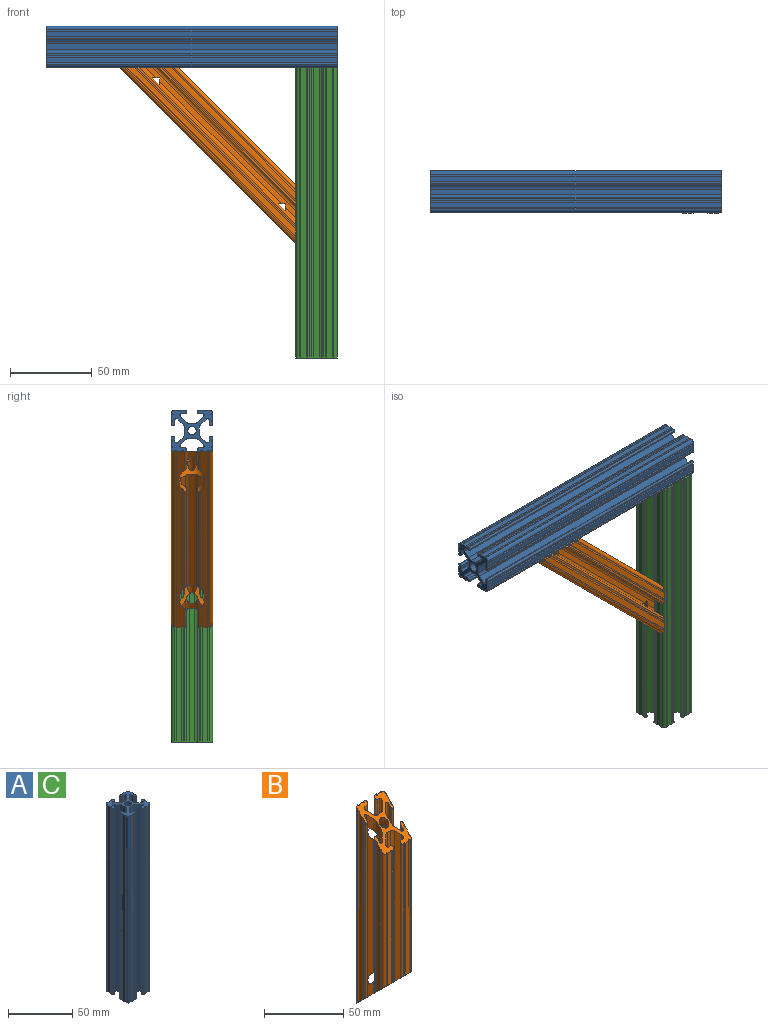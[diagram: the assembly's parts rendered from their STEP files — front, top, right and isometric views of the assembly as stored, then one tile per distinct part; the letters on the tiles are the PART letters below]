
ASSEMBLY  parts=3 mates=6
PART A: 99 faces, bbox 25.4x25.4x177.8 mm
  f0: cylinder r=2.6mm len=177.8mm, axis (0,0,-1), area 2908.5mm2, adj f97,f98
  f1: cylinder r=2.11mm len=177.8mm, axis (0,0,-1), area 597.8mm2, adj f88,f89,f97,f98
  f2: cylinder r=2.11mm len=177.8mm, axis (0,0,-1), area 597.8mm2, adj f65,f66,f97,f98
  f3: cylinder r=1.03mm len=177.8mm, axis (0,0,-1), area 433.3mm2, adj f57,f58,f97,f98
  f4: cylinder r=0.51mm len=177.8mm, axis (0,0,-1), area 283.7mm2, adj f42,f43,f97,f98
  f5: cylinder r=0.51mm len=177.8mm, axis (0,0,-1), area 283.8mm2, adj f41,f42,f97,f98
  f6: cylinder r=0.51mm len=177.8mm, axis (0,0,-1), area 283.8mm2, adj f24,f25,f97,f98
  f7: cylinder r=0.51mm len=177.8mm, axis (0,0,-1), area 283.7mm2, adj f23,f24,f97,f98
  f8: cylinder r=1.08mm len=177.8mm, axis (0,0,-1), area 452.8mm2, adj f9,f96,f97,f98
  f9: plane 177.8x3.23mm, normal (0.71,-0.71,0), area 810.8mm2, adj f8,f10,f97,f98
  f10: cylinder r=3.17mm len=177.8mm, axis (0,0,-1), area 442.9mm2, adj f9,f11,f97,f98
  f11: plane 177.8x3.42mm, normal (0,-1,0), area 607.8mm2, adj f10,f12,f97,f98
  f12: cylinder r=3.17mm len=177.8mm, axis (0,0,-1), area 442.9mm2, adj f11,f13,f97,f98
  f13: plane 177.8x3.23mm, normal (-0.71,-0.71,0), area 810.8mm2, adj f12,f14,f97,f98
  f14: cylinder r=1.08mm len=177.8mm, axis (0,0,-1), area 452.8mm2, adj f13,f15,f97,f98
  f15: plane 177.8x2.13mm, normal (0,1,0), area 378.5mm2, adj f14,f16,f97,f98
  f16: cylinder r=1.05mm len=177.8mm, axis (0,0,-1), area 293mm2, adj f15,f17,f97,f98
  f17: plane 177.8x0.11mm, normal (-1,0,0), area 19.9mm2, adj f16,f18,f97,f98
  f18: cylinder r=1.05mm len=177.8mm, axis (0,0,-1), area 293mm2, adj f17,f19,f97,f98
  f19: plane 177.8x1.03mm, normal (0,-1,0), area 183.1mm2, adj f18,f20,f97,f98
  f20: cylinder r=0.51mm len=177.8mm, axis (0,0,-1), area 283.8mm2, adj f19,f21,f97,f98
  f21: plane 177.8x3.22mm, normal (0,-1,0), area 572mm2, adj f20,f22,f97,f98
  f22: cylinder r=0.51mm len=177.8mm, axis (0,0,-1), area 283.7mm2, adj f21,f23,f97,f98
  f23: cylinder r=2.11mm len=177.8mm, axis (0,0,-1), area 597.8mm2, adj f7,f22,f97,f98
  f24: plane 177.8x3.22mm, normal (1,0,0), area 572mm2, adj f6,f7,f97,f98
  f25: plane 177.8x1.03mm, normal (1,0,0), area 183.1mm2, adj f6,f26,f97,f98
  f26: cylinder r=1.05mm len=177.8mm, axis (0,0,-1), area 293mm2, adj f25,f27,f97,f98
  f27: plane 177.8x0.11mm, normal (0,1,0), area 19.9mm2, adj f26,f28,f97,f98
  f28: cylinder r=1.05mm len=177.8mm, axis (0,0,-1), area 293mm2, adj f27,f29,f97,f98
  f29: plane 177.8x2.11mm, normal (-1,0,0), area 376mm2, adj f28,f30,f97,f98
  f30: cylinder r=1.03mm len=177.8mm, axis (0,0,-1), area 430.2mm2, adj f29,f31,f97,f98
  f31: plane 177.8x3.3mm, normal (0.71,0.71,0), area 827.9mm2, adj f30,f32,f97,f98
  f32: cylinder r=3.17mm len=177.8mm, axis (0,0,-1), area 444mm2, adj f31,f33,f97,f98
  f33: plane 177.8x3.19mm, normal (1,0,0), area 566.5mm2, adj f32,f34,f97,f98
  f34: cylinder r=3.17mm len=177.8mm, axis (0,0,-1), area 444mm2, adj f33,f35,f97,f98
  f35: plane 177.8x3.3mm, normal (0.71,-0.71,0), area 827.9mm2, adj f34,f36,f97,f98
  f36: cylinder r=1.03mm len=177.8mm, axis (0,0,-1), area 430.2mm2, adj f35,f37,f97,f98
  f37: plane 177.8x2.11mm, normal (-1,0,0), area 376mm2, adj f36,f38,f97,f98
  f38: cylinder r=1.05mm len=177.8mm, axis (0,0,-1), area 293mm2, adj f37,f39,f97,f98
  f39: plane 177.8x0.11mm, normal (0,-1,0), area 19.9mm2, adj f38,f40,f97,f98
  f40: cylinder r=1.05mm len=177.8mm, axis (0,0,-1), area 293mm2, adj f39,f41,f97,f98
  f41: plane 177.8x1.03mm, normal (1,0,0), area 183.1mm2, adj f5,f40,f97,f98
  f42: plane 177.8x3.22mm, normal (1,0,0), area 572mm2, adj f4,f5,f97,f98
  f43: cylinder r=2.11mm len=177.8mm, axis (0,0,-1), area 597.8mm2, adj f4,f44,f97,f98
  f44: cylinder r=0.51mm len=177.8mm, axis (0,0,-1), area 283.7mm2, adj f43,f45,f97,f98
  f45: plane 177.8x3.22mm, normal (0,1,0), area 572mm2, adj f44,f46,f97,f98
  f46: cylinder r=0.51mm len=177.8mm, axis (0,0,-1), area 283.8mm2, adj f45,f47,f97,f98
  f47: plane 177.8x1.03mm, normal (0,1,0), area 183.1mm2, adj f46,f48,f97,f98
  f48: cylinder r=1.05mm len=177.8mm, axis (0,0,-1), area 293mm2, adj f47,f49,f97,f98
  f49: plane 177.8x0.11mm, normal (-1,0,0), area 19.9mm2, adj f48,f50,f97,f98
  f50: cylinder r=1.05mm len=177.8mm, axis (0,0,-1), area 293mm2, adj f49,f51,f97,f98
  f51: plane 177.8x2.19mm, normal (0,-1,0), area 389.3mm2, adj f50,f52,f97,f98
  f52: cylinder r=1.03mm len=177.8mm, axis (0,0,-1), area 433.3mm2, adj f51,f53,f97,f98
  f53: plane 177.8x3.31mm, normal (-0.71,0.71,0), area 831mm2, adj f52,f54,f97,f98
  f54: cylinder r=3.17mm len=177.8mm, axis (0,0,-1), area 442.7mm2, adj f53,f55,f97,f98
  f55: plane 177.8x3.31mm, normal (0,1,0), area 588.8mm2, adj f54,f56,f97,f98
  f56: cylinder r=3.17mm len=177.8mm, axis (0,0,-1), area 442.7mm2, adj f55,f57,f97,f98
  f57: plane 177.8x3.31mm, normal (0.71,0.71,0), area 831mm2, adj f3,f56,f97,f98
  f58: plane 177.8x2.19mm, normal (0,-1,0), area 389.3mm2, adj f3,f59,f97,f98
  f59: cylinder r=1.05mm len=177.8mm, axis (0,0,-1), area 293mm2, adj f58,f60,f97,f98
  f60: plane 177.8x0.11mm, normal (1,0,0), area 19.9mm2, adj f59,f61,f97,f98
  f61: cylinder r=1.05mm len=177.8mm, axis (0,0,-1), area 293mm2, adj f60,f62,f97,f98
  f62: plane 177.8x1.03mm, normal (0,1,0), area 183.1mm2, adj f61,f63,f97,f98
  f63: cylinder r=0.51mm len=177.8mm, axis (0,0,-1), area 283.8mm2, adj f62,f64,f97,f98
  f64: plane 177.8x3.22mm, normal (0,1,0), area 572mm2, adj f63,f65,f97,f98
  f65: cylinder r=0.51mm len=177.8mm, axis (0,0,-1), area 283.7mm2, adj f2,f64,f97,f98
  f66: cylinder r=0.51mm len=177.8mm, axis (0,0,-1), area 283.7mm2, adj f2,f67,f97,f98
  f67: plane 177.8x3.22mm, normal (-1,0,0), area 572mm2, adj f66,f68,f97,f98
  f68: cylinder r=0.51mm len=177.8mm, axis (0,0,-1), area 283.8mm2, adj f67,f69,f97,f98
  f69: plane 177.8x1.03mm, normal (-1,0,0), area 183.1mm2, adj f68,f70,f97,f98
  f70: cylinder r=1.05mm len=177.8mm, axis (0,0,-1), area 293mm2, adj f69,f71,f97,f98
  f71: plane 177.8x0.11mm, normal (0,-1,0), area 19.9mm2, adj f70,f72,f97,f98
  f72: cylinder r=1.05mm len=177.8mm, axis (0,0,-1), area 293mm2, adj f71,f73,f97,f98
  f73: plane 177.8x2.11mm, normal (1,0,0), area 376mm2, adj f72,f74,f97,f98
  f74: cylinder r=1.03mm len=177.8mm, axis (0,0,-1), area 430.2mm2, adj f73,f75,f97,f98
  f75: plane 177.8x3.3mm, normal (-0.71,-0.71,0), area 827.9mm2, adj f74,f76,f97,f98
  f76: cylinder r=3.17mm len=177.8mm, axis (0,0,-1), area 444mm2, adj f75,f77,f97,f98
  f77: plane 177.8x3.19mm, normal (-1,0,0), area 566.5mm2, adj f76,f78,f97,f98
  f78: cylinder r=3.17mm len=177.8mm, axis (0,0,-1), area 444mm2, adj f77,f79,f97,f98
  f79: plane 177.8x3.3mm, normal (-0.71,0.71,0), area 827.9mm2, adj f78,f80,f97,f98
  f80: cylinder r=1.03mm len=177.8mm, axis (0,0,-1), area 430.2mm2, adj f79,f81,f97,f98
  f81: plane 177.8x2.11mm, normal (1,0,0), area 376mm2, adj f80,f82,f97,f98
  f82: cylinder r=1.05mm len=177.8mm, axis (0,0,-1), area 293mm2, adj f81,f83,f97,f98
  f83: plane 177.8x0.11mm, normal (0,1,0), area 19.9mm2, adj f82,f84,f97,f98
  f84: cylinder r=1.05mm len=177.8mm, axis (0,0,-1), area 293mm2, adj f83,f85,f97,f98
  f85: plane 177.8x1.03mm, normal (-1,0,0), area 183.1mm2, adj f84,f86,f97,f98
  f86: cylinder r=0.51mm len=177.8mm, axis (0,0,-1), area 283.8mm2, adj f85,f87,f97,f98
  f87: plane 177.8x3.22mm, normal (-1,0,0), area 572mm2, adj f86,f88,f97,f98
  f88: cylinder r=0.51mm len=177.8mm, axis (0,0,-1), area 283.7mm2, adj f1,f87,f97,f98
  f89: cylinder r=0.51mm len=177.8mm, axis (0,0,-1), area 283.7mm2, adj f1,f90,f97,f98
  f90: plane 177.8x3.22mm, normal (0,-1,0), area 572mm2, adj f89,f91,f97,f98
  f91: cylinder r=0.51mm len=177.8mm, axis (0,0,-1), area 283.8mm2, adj f90,f92,f97,f98
  f92: plane 177.8x1.03mm, normal (0,-1,0), area 183.1mm2, adj f91,f93,f97,f98
  f93: cylinder r=1.05mm len=177.8mm, axis (0,0,-1), area 293mm2, adj f92,f94,f97,f98
  f94: plane 177.8x0.11mm, normal (1,0,0), area 19.9mm2, adj f93,f95,f97,f98
  f95: cylinder r=1.05mm len=177.8mm, axis (0,0,-1), area 293mm2, adj f94,f96,f97,f98
  f96: plane 177.8x2.13mm, normal (0,1,0), area 378.5mm2, adj f8,f95,f97,f98
  f97: plane 25.4x25.4mm, normal (0,0,-1), area 280.1mm2, adj f0,f1,f2,f3,f4,f5,f6,f7
  f98: plane 25.4x25.4mm, normal (0,0,1), area 280.1mm2, adj f0,f1,f2,f3,f4,f5,f6,f7
PART B: 161 faces, bbox 26.7x36.6x153.7 mm
  f0: cylinder r=3.26mm len=8.96mm, axis (0,0.71,0.71), area 83.2mm2, adj f1,f2,f154,f155,f156,f157,f158,f159
  f1: cylinder r=2.6mm len=3.41mm, axis (0,0,-1), area 0.1mm2, adj f0,f160
  f2: plane 9.13x9.13mm, normal (0,0.71,0.71), area 27.8mm2, adj f0,f3,f150,f151,f152,f153,f154,f159
  f3: plane 12.81x3.37mm, normal (-0.71,0.71,0), area 44.2mm2, adj f2,f4,f153,f154,f160
  f4: cylinder r=1.03mm len=16.44mm, axis (0,0,-1), area 36.1mm2, adj f3,f5,f153,f160
  f5: plane 14.49x2.19mm, normal (0,-1,0), area 28.1mm2, adj f4,f6,f153,f160
  f6: cylinder r=1.05mm len=12.83mm, axis (0,0,-1), area 20.1mm2, adj f5,f7,f153,f160
  f7: plane 13.05x0.11mm, normal (-1,0,0), area 1.4mm2, adj f6,f8,f153,f160
  f8: cylinder r=1.05mm len=15.95mm, axis (0,0,-1), area 24.2mm2, adj f7,f9,f149,f153,f160
  f9: plane 1.05x0mm, normal (0,0,-1), area 0mm2, adj f8,f10,f149,f160
  f10: cylinder r=0.51mm len=18.63mm, axis (0,0,-1), area 28.5mm2, adj f9,f11,f148,f149,f153,f160
  f11: plane 152.4x3.22mm, normal (0,1,0), area 460.7mm2, adj f10,f12,f143,f144,f145,f147,f148,f153
  f12: cylinder r=0.51mm len=152.4mm, axis (0,0,-1), area 243.2mm2, adj f11,f13,f23,f143,f148,f160
  f13: cylinder r=2.11mm len=152.4mm, axis (0,0,-1), area 507.2mm2, adj f12,f14,f23,f160
  f14: cylinder r=0.51mm len=148.13mm, axis (0,0,-1), area 234.8mm2, adj f13,f15,f23,f160
  f15: plane 146.1x3.22mm, normal (1,0,0), area 459.7mm2, adj f14,f16,f23,f160
  f16: cylinder r=0.51mm len=139.67mm, axis (0,0,-1), area 221.3mm2, adj f15,f17,f23,f160
  f17: plane 137.63x1.03mm, normal (1,0,0), area 140.7mm2, adj f16,f18,f23,f160
  f18: cylinder r=1.05mm len=135.58mm, axis (0,0,-1), area 221.7mm2, adj f17,f19,f23,f160
  f19: plane 133.48x0.11mm, normal (0,-1,0), area 14.9mm2, adj f18,f20,f23,f160
  f20: cylinder r=1.05mm len=135.58mm, axis (0,0,-1), area 221.7mm2, adj f19,f21,f23,f160
  f21: plane 139.8x2.11mm, normal (-1,0,0), area 291.2mm2, adj f20,f22,f23,f160
  f22: cylinder r=1.03mm len=141.26mm, axis (0,0,-1), area 340mm2, adj f21,f23,f150,f160
  f23: plane 26.67x26.67mm, normal (0,-0.71,0.71), area 390.8mm2, adj f12,f13,f14,f15,f16,f17,f18,f19
  f24: cylinder r=3.26mm len=8.96mm, axis (0,0.71,-0.71), area 83.2mm2, adj f23,f25,f26,f27,f28,f117,f118,f119
  f25: cylinder r=2.6mm len=6.2mm, axis (0,0,-1), area 9mm2, adj f24,f26,f159
  f26: plane 9.13x9.13mm, normal (0,0.71,-0.71), area 27.8mm2, adj f24,f25,f62,f65,f66,f116,f117,f145
  f27: plane 9.13x9.13mm, normal (0,0.71,-0.71), area 27.8mm2, adj f24,f119,f120,f128,f145,f150,f152,f159
  f28: cylinder r=2.6mm len=3.41mm, axis (0,0,-1), area 0.1mm2, adj f23,f24
  f29: cylinder r=0.51mm len=101.6mm, axis (0,0,-1), area 162.1mm2, adj f23,f30,f142,f160
  f30: plane 101.6x1.03mm, normal (0,-1,0), area 104.6mm2, adj f23,f29,f31,f160
  f31: cylinder r=1.05mm len=103.7mm, axis (0,0,-1), area 169.1mm2, adj f23,f30,f32,f160
  f32: plane 103.92x0.11mm, normal (-1,0,0), area 11.6mm2, adj f23,f31,f33,f160
  f33: cylinder r=1.05mm len=106.02mm, axis (0,0,-1), area 173mm2, adj f23,f32,f34,f160
  f34: plane 106.02x2.13mm, normal (0,1,0), area 225.7mm2, adj f23,f33,f35,f160
  f35: cylinder r=1.08mm len=109.71mm, axis (0,0,-1), area 274.7mm2, adj f23,f34,f36,f160
  f36: plane 116.15x3.23mm, normal (-0.71,-0.71,0), area 515mm2, adj f23,f35,f37,f160
  f37: cylinder r=3.17mm len=118.01mm, axis (0,0,-1), area 291.6mm2, adj f23,f36,f38,f160
  f38: plane 118.01x3.42mm, normal (0,-1,0), area 403.4mm2, adj f23,f37,f39,f160
  f39: cylinder r=3.17mm len=118.01mm, axis (0,0,-1), area 291.6mm2, adj f23,f38,f40,f160
  f40: plane 116.15x3.23mm, normal (0.71,-0.71,0), area 515mm2, adj f23,f39,f41,f160
  f41: cylinder r=1.08mm len=109.71mm, axis (0,0,-1), area 274.3mm2, adj f23,f40,f42,f160
  f42: plane 106.02x2.13mm, normal (0,1,0), area 225.7mm2, adj f23,f41,f43,f160
  f43: cylinder r=1.05mm len=106.02mm, axis (0,0,-1), area 173mm2, adj f23,f42,f44,f160
  f44: plane 103.92x0.11mm, normal (1,0,0), area 11.6mm2, adj f23,f43,f45,f160
  f45: cylinder r=1.05mm len=103.7mm, axis (0,0,-1), area 169.1mm2, adj f23,f44,f46,f160
  f46: plane 101.6x1.03mm, normal (0,-1,0), area 104.6mm2, adj f23,f45,f47,f160
  f47: cylinder r=0.51mm len=101.6mm, axis (0,0,-1), area 162.1mm2, adj f23,f46,f48,f160
  f48: plane 101.6x3.22mm, normal (0,-1,0), area 326.9mm2, adj f23,f47,f49,f160
  f49: cylinder r=0.51mm len=101.6mm, axis (0,0,-1), area 162.1mm2, adj f23,f48,f50,f160
  f50: cylinder r=2.11mm len=105.87mm, axis (0,0,-1), area 346.8mm2, adj f23,f49,f51,f160
  f51: cylinder r=0.51mm len=107.9mm, axis (0,0,-1), area 170.6mm2, adj f23,f50,f52,f160
  f52: plane 114.33x3.22mm, normal (-1,0,0), area 357.5mm2, adj f23,f51,f53,f160
  f53: cylinder r=0.51mm len=116.37mm, axis (0,0,-1), area 184.1mm2, adj f23,f52,f54,f160
  f54: plane 118.43x1.03mm, normal (-1,0,0), area 120.9mm2, adj f23,f53,f55,f160
  f55: cylinder r=1.05mm len=120.52mm, axis (0,0,-1), area 196.9mm2, adj f23,f54,f56,f160
  f56: plane 120.52x0.11mm, normal (0,1,0), area 13.5mm2, adj f23,f55,f57,f160
  f57: cylinder r=1.05mm len=120.52mm, axis (0,0,-1), area 196.9mm2, adj f23,f56,f58,f160
  f58: plane 118.43x2.11mm, normal (1,0,0), area 246mm2, adj f23,f57,f59,f160
  f59: cylinder r=1.03mm len=114.2mm, axis (0,0,-1), area 274.5mm2, adj f23,f58,f60,f160
  f60: plane 119.32x3.3mm, normal (-0.71,0.71,0), area 540.2mm2, adj f23,f59,f61,f160
  f61: cylinder r=3.17mm len=123.81mm, axis (0,0,-1), area 303.6mm2, adj f23,f60,f62,f160
  f62: plane 130.19x3.19mm, normal (-1,0,0), area 398.7mm2, adj f23,f26,f61,f63,f64,f65,f145,f153
  f63: cylinder r=3.17mm len=11.23mm, axis (0,0,-1), area 22.4mm2, adj f62,f66,f157,f160
  f64: cylinder r=3.17mm len=105.34mm, axis (0,0,-1), area 260.1mm2, adj f62,f66,f145,f153
  f65: cylinder r=3.17mm len=11.23mm, axis (0,0,-1), area 22.4mm2, adj f23,f26,f62,f66
  f66: plane 141.26x3.3mm, normal (-0.71,-0.71,0), area 595.3mm2, adj f23,f26,f63,f64,f65,f67,f145,f153
  f67: cylinder r=1.03mm len=141.26mm, axis (0,0,-1), area 340mm2, adj f23,f66,f68,f160
  f68: plane 139.8x2.11mm, normal (1,0,0), area 291.2mm2, adj f23,f67,f69,f160
  f69: cylinder r=1.05mm len=135.58mm, axis (0,0,-1), area 221.7mm2, adj f23,f68,f70,f160
  f70: plane 133.48x0.11mm, normal (0,-1,0), area 14.9mm2, adj f23,f69,f71,f160
  f71: cylinder r=1.05mm len=135.58mm, axis (0,0,-1), area 221.7mm2, adj f23,f70,f72,f160
  f72: plane 137.63x1.03mm, normal (-1,0,0), area 140.7mm2, adj f23,f71,f73,f160
  f73: cylinder r=0.51mm len=139.67mm, axis (0,0,-1), area 221.3mm2, adj f23,f72,f74,f160
  f74: plane 146.1x3.22mm, normal (-1,0,0), area 459.7mm2, adj f23,f73,f75,f160
  f75: cylinder r=0.51mm len=148.13mm, axis (0,0,-1), area 234.8mm2, adj f23,f74,f76,f160
  f76: cylinder r=2.11mm len=152.4mm, axis (0,0,-1), area 507.2mm2, adj f23,f75,f77,f160
  f77: cylinder r=0.51mm len=152.4mm, axis (0,0,-1), area 243.2mm2, adj f23,f76,f78,f88,f107,f160
  f78: plane 3.22x0mm, normal (0,0,-1), area 0mm2, adj f77,f79,f88,f160
  f79: cylinder r=0.51mm len=18.63mm, axis (0,0,-1), area 28.5mm2, adj f78,f80,f87,f88,f153,f160
  f80: plane 17.11x1.07mm, normal (0,1,0), area 17mm2, adj f79,f81,f87,f153
  f81: cylinder r=1.05mm len=15.95mm, axis (0,0,-1), area 24.2mm2, adj f80,f82,f87,f153,f160
  f82: plane 13.05x0.11mm, normal (1,0,0), area 1.4mm2, adj f81,f83,f153,f160
  f83: cylinder r=1.05mm len=12.83mm, axis (0,0,-1), area 20.1mm2, adj f82,f84,f153,f160
  f84: plane 14.49x2.19mm, normal (0,-1,0), area 28.1mm2, adj f83,f85,f153,f160
  f85: cylinder r=1.03mm len=16.32mm, axis (0,0,-1), area 35.6mm2, adj f84,f86,f153,f160
  f86: plane 12.81x3.37mm, normal (0.71,0.71,0), area 44.2mm2, adj f85,f153,f156,f157,f160
  f87: plane 1.05x0mm, normal (0,0,-1), area 0mm2, adj f79,f80,f81,f160
  f88: plane 152.4x3.22mm, normal (0,1,0), area 460.7mm2, adj f77,f78,f79,f89,f107,f108,f145,f153
  f89: cylinder r=0.51mm len=88.07mm, axis (0,0,-1), area 138mm2, adj f88,f90,f145,f153
  f90: plane 84.97x1.07mm, normal (0,1,0), area 86.2mm2, adj f89,f91,f145,f153
  f91: cylinder r=1.05mm len=83.2mm, axis (0,0,-1), area 136.7mm2, adj f90,f92,f145,f153
  f92: plane 83.43x0.11mm, normal (1,0,0), area 9.3mm2, adj f91,f93,f145,f153
  f93: cylinder r=1.05mm len=87.13mm, axis (0,0,-1), area 140.5mm2, adj f92,f94,f145,f153
  f94: plane 93.04x2.19mm, normal (0,-1,0), area 196.4mm2, adj f93,f95,f145,f153
  f95: cylinder r=1.03mm len=100.83mm, axis (0,0,-1), area 239.1mm2, adj f94,f96,f145,f153
  f96: plane 100.14x3.31mm, normal (0.71,0.71,0), area 454.8mm2, adj f95,f97,f145,f153
  f97: cylinder r=3.17mm len=96.6mm, axis (0,0,-1), area 239.8mm2, adj f96,f98,f145,f153
  f98: plane 96.05x3.31mm, normal (0,1,0), area 317mm2, adj f97,f99,f145,f153
  f99: cylinder r=3.17mm len=96.6mm, axis (0,0,-1), area 239.8mm2, adj f98,f100,f145,f153
  f100: plane 100.14x3.31mm, normal (-0.71,0.71,0), area 454.8mm2, adj f99,f101,f145,f153
  f101: cylinder r=1.03mm len=100.14mm, axis (0,0,-1), area 235.4mm2, adj f100,f102,f145,f153
  f102: plane 93.04x2.19mm, normal (0,-1,0), area 196.4mm2, adj f101,f103,f145,f153
  f103: cylinder r=1.05mm len=87.13mm, axis (0,0,-1), area 140.5mm2, adj f102,f104,f145,f153
  f104: plane 83.43x0.11mm, normal (-1,0,0), area 9.3mm2, adj f103,f105,f145,f153
  f105: cylinder r=1.05mm len=83.2mm, axis (0,0,-1), area 136.7mm2, adj f104,f106,f145,f153
  f106: plane 84.97x1.07mm, normal (0,1,0), area 86.2mm2, adj f105,f145,f147,f153
  f107: plane 3.22x0mm, normal (0,0,1), area 0mm2, adj f23,f77,f88,f108
  f108: cylinder r=0.51mm len=18.63mm, axis (0,0,-1), area 28.5mm2, adj f23,f88,f107,f109,f110,f145
  f109: plane 17.11x1.07mm, normal (0,1,0), area 17mm2, adj f108,f110,f111,f145
  f110: plane 1.05x0mm, normal (0,0,1), area 0mm2, adj f23,f108,f109,f111
  f111: cylinder r=1.05mm len=15.95mm, axis (0,0,-1), area 24.2mm2, adj f23,f109,f110,f112,f145
  f112: plane 13.05x0.11mm, normal (1,0,0), area 1.4mm2, adj f23,f111,f113,f145
  f113: cylinder r=1.05mm len=12.83mm, axis (0,0,-1), area 20.1mm2, adj f23,f112,f114,f145
  f114: plane 14.49x2.19mm, normal (0,-1,0), area 28.1mm2, adj f23,f113,f115,f145
  f115: cylinder r=1.03mm len=16.32mm, axis (0,0,-1), area 35.6mm2, adj f23,f114,f116,f145
  f116: plane 12.81x3.37mm, normal (0.71,0.71,0), area 44.2mm2, adj f23,f26,f115,f117,f145
  f117: cylinder r=3.17mm len=9.5mm, axis (0,0,-1), area 19.4mm2, adj f23,f24,f26,f116,f118
  f118: plane 5.24x3.53mm, normal (0,1,0), area 15.2mm2, adj f23,f24,f117,f119
  f119: cylinder r=3.17mm len=9.5mm, axis (0,0,-1), area 19.4mm2, adj f23,f24,f27,f118,f120
  f120: plane 12.81x3.37mm, normal (-0.71,0.71,0), area 44.2mm2, adj f23,f27,f119,f121,f145
  f121: cylinder r=1.03mm len=16.44mm, axis (0,0,-1), area 36.1mm2, adj f23,f120,f122,f145
  f122: plane 14.49x2.19mm, normal (0,-1,0), area 28.1mm2, adj f23,f121,f123,f145
  f123: cylinder r=1.05mm len=12.83mm, axis (0,0,-1), area 20.1mm2, adj f23,f122,f124,f145
  f124: plane 13.05x0.11mm, normal (-1,0,0), area 1.4mm2, adj f23,f123,f125,f145
  f125: cylinder r=1.05mm len=15.95mm, axis (0,0,-1), area 24.2mm2, adj f23,f124,f126,f127,f145
  f126: plane 17.11x1.07mm, normal (0,1,0), area 17mm2, adj f125,f127,f144,f145
  f127: plane 1.05x0mm, normal (0,0,1), area 0mm2, adj f23,f125,f126,f144
  f128: cylinder r=3.17mm len=11.23mm, axis (0,0,-1), area 22.4mm2, adj f23,f27,f150,f152
  f129: cylinder r=3.17mm len=123.81mm, axis (0,0,-1), area 303.6mm2, adj f23,f130,f152,f160
  f130: plane 119.32x3.3mm, normal (0.71,0.71,0), area 540.2mm2, adj f23,f129,f131,f160
  f131: cylinder r=1.03mm len=114.2mm, axis (0,0,-1), area 274.5mm2, adj f23,f130,f132,f160
  f132: plane 118.43x2.11mm, normal (-1,0,0), area 246mm2, adj f23,f131,f133,f160
  f133: cylinder r=1.05mm len=120.52mm, axis (0,0,-1), area 196.9mm2, adj f23,f132,f134,f160
  f134: plane 120.52x0.11mm, normal (0,1,0), area 13.5mm2, adj f23,f133,f135,f160
  f135: cylinder r=1.05mm len=120.52mm, axis (0,0,-1), area 196.9mm2, adj f23,f134,f136,f160
  f136: plane 118.43x1.03mm, normal (1,0,0), area 120.9mm2, adj f23,f135,f137,f160
  f137: cylinder r=0.51mm len=116.37mm, axis (0,0,-1), area 184.1mm2, adj f23,f136,f138,f160
  f138: plane 114.33x3.22mm, normal (1,0,0), area 357.5mm2, adj f23,f137,f139,f160
  f139: cylinder r=0.51mm len=107.9mm, axis (0,0,-1), area 170.6mm2, adj f23,f138,f140,f160
  f140: cylinder r=2.11mm len=105.87mm, axis (0,0,-1), area 348.8mm2, adj f23,f139,f141,f160
  f141: cylinder r=0.51mm len=101.6mm, axis (0,0,-1), area 162.1mm2, adj f23,f140,f142,f160
  f142: plane 101.6x3.22mm, normal (0,-1,0), area 326.9mm2, adj f23,f29,f141,f160
  f143: plane 3.22x0mm, normal (0,0,1), area 0mm2, adj f11,f12,f23,f144
  f144: cylinder r=0.51mm len=18.63mm, axis (0,0,-1), area 28.5mm2, adj f11,f23,f126,f127,f143,f145
  f145: cylinder r=7.94mm len=23.76mm, axis (0,0.71,-0.71), area 283.8mm2, adj f11,f26,f27,f62,f64,f66,f88,f89
  f146: cylinder r=3.17mm len=105.34mm, axis (0,0,-1), area 260.1mm2, adj f145,f150,f152,f153
  f147: cylinder r=0.51mm len=88.07mm, axis (0,0,-1), area 138mm2, adj f11,f106,f145,f153
  f148: plane 3.22x0mm, normal (0,0,-1), area 0mm2, adj f10,f11,f12,f160
  f149: plane 17.11x1.07mm, normal (0,1,0), area 17mm2, adj f8,f9,f10,f153
  f150: plane 141.26x3.3mm, normal (0.71,-0.71,0), area 595.3mm2, adj f2,f22,f23,f27,f128,f145,f146,f151
  f151: cylinder r=3.17mm len=11.23mm, axis (0,0,-1), area 22.4mm2, adj f2,f150,f152,f160
  f152: plane 130.19x3.19mm, normal (1,0,0), area 398.7mm2, adj f2,f23,f27,f128,f129,f145,f146,f151
  f153: cylinder r=7.94mm len=23.76mm, axis (0,0.71,0.71), area 283.5mm2, adj f2,f3,f4,f5,f6,f7,f8,f10
  f154: cylinder r=3.17mm len=9.5mm, axis (0,0,-1), area 19.4mm2, adj f0,f2,f3,f155,f160
  f155: plane 5.24x3.53mm, normal (0,1,0), area 15.2mm2, adj f0,f154,f156,f160
  f156: cylinder r=3.17mm len=9.5mm, axis (0,0,-1), area 19.4mm2, adj f0,f86,f155,f157,f160
  f157: plane 9.13x9.13mm, normal (0,0.71,0.71), area 27.8mm2, adj f0,f62,f63,f66,f86,f153,f156,f158
  f158: cylinder r=2.6mm len=6.2mm, axis (0,0,-1), area 9mm2, adj f0,f157,f159
  f159: cylinder r=2.6mm len=123.06mm, axis (0,0,-1), area 1848mm2, adj f0,f2,f23,f24,f25,f26,f27,f145
  f160: plane 26.67x26.67mm, normal (0,-0.71,-0.71), area 390.8mm2, adj f0,f1,f3,f4,f5,f6,f7,f8
PART C: same geometry as A
PLACE A rot(axis=(0,1,0),90deg) t=(65.76,84.04,159.72)mm
PLACE B rot(axis=(-0.36,-0.36,0.86),98.4deg) t=(20.86,84.04,102.12)mm
PLACE C t=(78.46,84.04,121.62)mm fixed
MATE planar C.f98 <-> A.f24  axis (0,0,1) through (67.97,77.64,147.02)mm
MATE planar A.f1 <-> C.f24  axis (1,0,0) through (91.16,73.45,170.31)mm
MATE planar B.f23 <-> A.f24  axis (0,0,1) through (-24.06,84.04,147.02)mm
MATE planar B.f74 <-> A.f21  axis (0,-1,0) through (15.23,71.34,96.5)mm
MATE planar C.f87 <-> B.f160  axis (-1,0,0) through (65.76,76.1,58.12)mm
MATE planar A.f90 <-> C.f90  axis (0,-1,0) through (2.26,71.34,167.66)mm
